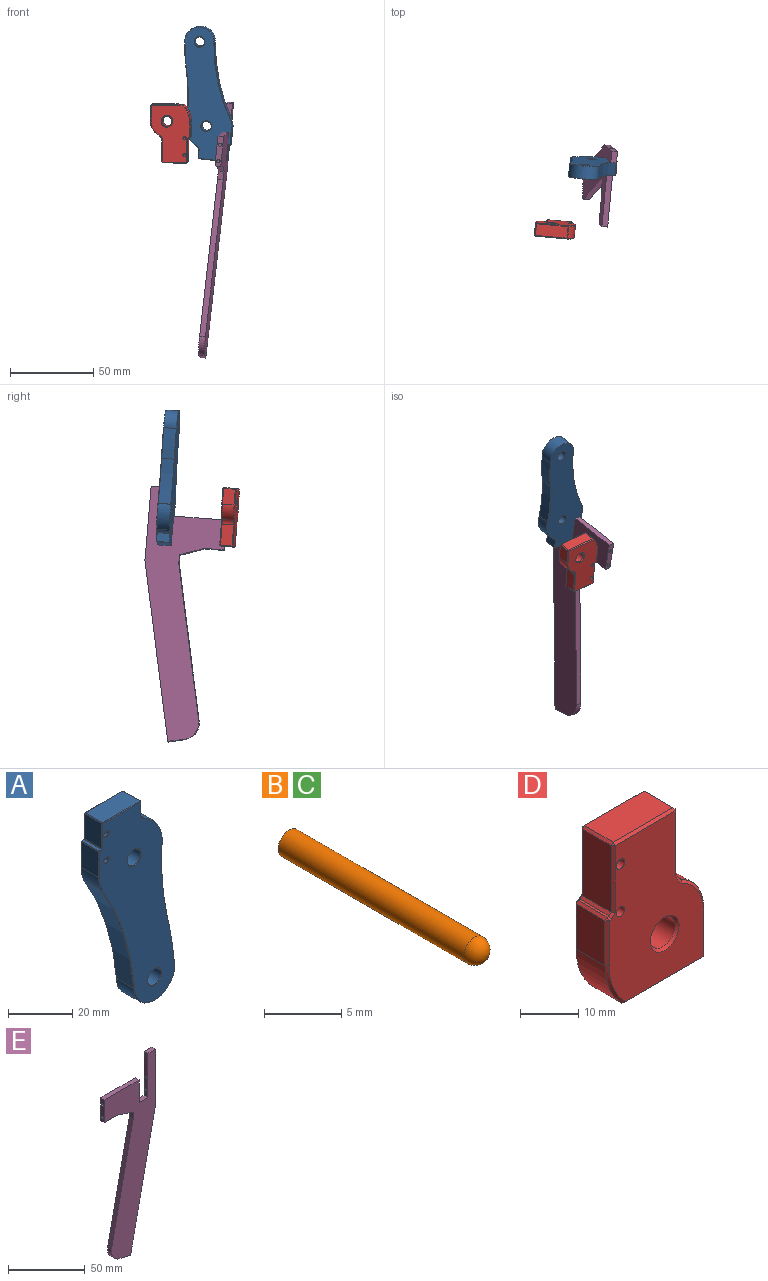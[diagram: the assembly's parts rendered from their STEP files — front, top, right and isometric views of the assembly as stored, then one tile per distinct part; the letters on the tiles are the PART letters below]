
ASSEMBLY  parts=5 mates=4
PART A: 80 faces, bbox 33.5x8x79 mm
  f0: plane 16.6x7.6mm, normal (0,0,1), area 126.2mm2, adj f45,f46,f56,f57
  f1: plane 9.6x7.6mm, normal (-1,0,0), area 73mm2, adj f55,f56,f65,f66
  f2: plane 7.6x1.1mm, normal (0,0,1), area 8.4mm2, adj f60,f65,f68,f71
  f3: plane 9.8x7.6mm, normal (-1,0,0), area 74.5mm2, adj f4,f59,f67,f68
  f4: cylinder r=14mm len=7.6mm, axis (0,1,0), area 37.8mm2, adj f3,f53,f54,f63
  f5: cylinder r=106mm len=45.07mm, axis (0,1,0), area 363.2mm2, adj f43,f44,f52,f53
  f6: cylinder r=9mm len=18mm, axis (0,1,0), area 234mm2, adj f33,f34,f42,f43
  f7: cylinder r=130mm len=18.19mm, axis (0,1,0), area 140.3mm2, adj f24,f25,f32,f33
  f8: cylinder r=106mm len=26.98mm, axis (0,1,0), area 206.3mm2, adj f18,f22,f23,f24
  f9: cylinder r=14mm len=14.77mm, axis (0,1,0), area 134.6mm2, adj f10,f21,f22,f31
  f10: cylinder r=4mm len=7.6mm, axis (0,1,0), area 20.1mm2, adj f9,f26,f36,f37
  f11: cylinder r=1mm len=7.6mm, axis (0,1,0), area 47.8mm2, adj f72,f74
  f12: cylinder r=1mm len=7.6mm, axis (0,1,0), area 47.8mm2, adj f73,f75
  f13: cylinder r=3mm len=7.6mm, axis (0,1,0), area 143.3mm2, adj f77,f78
  f14: cylinder r=3mm len=7.6mm, axis (0,1,0), area 143.3mm2, adj f76,f79
  f15: plane 7.6x5.37mm, normal (1,0,0), area 40.8mm2, adj f35,f36,f46,f47
  f16: plane 78.6x33.1mm, normal (0,-1,0), area 1498.9mm2, adj f23,f27,f28,f31,f32,f37,f38,f41
  f17: plane 78.6x33.1mm, normal (0,1,0), area 1498.9mm2, adj f18,f19,f20,f21,f25,f26,f29,f30
  f18: cone r=106.2mm half-angle=45deg, axis (0,1,0), area 7.7mm2, adj f8,f17,f19,f20
  f19: plane 0.2x0.2mm, normal (0.7,0.71,-0.07), area 0mm2, adj f17,f18,f21,f22
  f20: plane 0.2x0.2mm, normal (0.69,0.71,0.16), area 0mm2, adj f17,f18,f24,f25
  f21: cone r=14mm half-angle=45deg, axis (0,-1,0), area 5mm2, adj f9,f17,f19,f26
  f22: plane 7.6x0.02mm, normal (0.99,0,-0.1), area 0.2mm2, adj f8,f9,f19,f27
  f23: cone r=106mm half-angle=45deg, axis (0,-1,0), area 7.7mm2, adj f8,f16,f27,f28
  f24: plane 7.6x0.01mm, normal (0.97,0,0.22), area 0mm2, adj f7,f8,f20,f28
  f25: cone r=130mm half-angle=45deg, axis (0,-1,0), area 5.2mm2, adj f7,f17,f20,f29
  f26: cone r=4.2mm half-angle=45deg, axis (0,1,0), area 0.8mm2, adj f10,f17,f21,f30
  f27: plane 0.2x0.2mm, normal (0.7,-0.71,-0.07), area 0mm2, adj f16,f22,f23,f31
  f28: plane 0.2x0.2mm, normal (0.69,-0.71,0.16), area 0mm2, adj f16,f23,f24,f32
  f29: plane 0.21x0.2mm, normal (0.7,0.71,0.13), area 0mm2, adj f17,f25,f33,f34
  f30: plane 0.22x0.2mm, normal (0.7,0.7,0.16), area 0mm2, adj f17,f26,f35,f36
  f31: cone r=13.8mm half-angle=45deg, axis (0,1,0), area 5mm2, adj f9,f16,f27,f37
  f32: cone r=129.8mm half-angle=45deg, axis (0,1,0), area 5.2mm2, adj f7,f16,f28,f38
  f33: plane 7.6x0.04mm, normal (0.98,0,0.19), area 0.3mm2, adj f6,f7,f29,f38
  f34: cone r=9mm half-angle=45deg, axis (0,-1,0), area 8.6mm2, adj f6,f17,f29,f39
  f35: plane 5.37x0.2mm, normal (0.71,0.71,0), area 1.5mm2, adj f15,f17,f30,f40
  f36: plane 7.6x0.09mm, normal (0.98,0,0.22), area 0.7mm2, adj f10,f15,f30,f41
  f37: cone r=4mm half-angle=45deg, axis (0,-1,0), area 0.8mm2, adj f10,f16,f31,f41
  f38: plane 0.21x0.2mm, normal (0.7,-0.71,0.13), area 0mm2, adj f16,f32,f33,f42
  f39: plane 0.2x0.2mm, normal (-0.71,0.71,-0.03), area 0mm2, adj f17,f34,f43,f44
  f40: plane 0.2x0.2mm, normal (0.58,0.58,0.58), area 0mm2, adj f35,f45,f46
  f41: plane 0.22x0.2mm, normal (0.7,-0.7,0.16), area 0mm2, adj f16,f36,f37,f47
  f42: cone r=8.8mm half-angle=45deg, axis (0,1,0), area 8.6mm2, adj f6,f16,f38,f48
  f43: plane 7.6x0.02mm, normal (-1,0,-0.04), area 0.1mm2, adj f5,f6,f39,f48
  f44: cone r=106.2mm half-angle=45deg, axis (0,1,0), area 13.5mm2, adj f5,f17,f39,f49
  f45: plane 16.6x0.2mm, normal (0,0.71,0.71), area 4.7mm2, adj f0,f17,f40,f50
  f46: plane 7.6x0.2mm, normal (0.71,0,0.71), area 2.1mm2, adj f0,f15,f40,f51
  f47: plane 5.37x0.2mm, normal (0.71,-0.71,0), area 1.5mm2, adj f15,f16,f41,f51
  f48: plane 0.2x0.2mm, normal (-0.71,-0.71,-0.03), area 0mm2, adj f16,f42,f43,f52
  f49: plane 0.2x0.19mm, normal (-0.64,0.71,-0.31), area 0mm2, adj f44,f53,f54
  f50: plane 0.2x0.2mm, normal (-0.58,0.58,0.58), area 0mm2, adj f45,f55,f56
  f51: plane 0.2x0.2mm, normal (0.58,-0.58,0.58), area 0mm2, adj f46,f47,f57
  f52: cone r=106mm half-angle=45deg, axis (0,-1,0), area 13.5mm2, adj f5,f16,f48,f58
  f53: plane 7.6x0.03mm, normal (-0.9,0,-0.43), area 0.3mm2, adj f4,f5,f49,f58
  f54: cone r=14mm half-angle=45deg, axis (0,-1,0), area 1.4mm2, adj f4,f17,f49,f59
  f55: plane 9.6x0.2mm, normal (-0.71,0.71,0), area 2.7mm2, adj f1,f17,f50,f61
  f56: plane 7.6x0.2mm, normal (-0.71,0,0.71), area 2.1mm2, adj f0,f1,f50,f62
  f57: plane 16.6x0.2mm, normal (0,-0.71,0.71), area 4.7mm2, adj f0,f16,f51,f62
  f58: plane 0.2x0.19mm, normal (-0.64,-0.71,-0.31), area 0mm2, adj f52,f53,f63
  f59: plane 9.8x0.2mm, normal (-0.71,0.71,0), area 2.8mm2, adj f3,f17,f54,f64
  f60: plane 1.1x0.2mm, normal (0,0.71,0.71), area 0.3mm2, adj f2,f17,f61,f64
  f61: plane 0.4x0.4mm, normal (-0.58,0.58,0.58), area 0.1mm2, adj f17,f55,f60,f65
  f62: plane 0.2x0.2mm, normal (-0.58,-0.58,0.58), area 0mm2, adj f56,f57,f66
  f63: cone r=13.8mm half-angle=45deg, axis (0,1,0), area 1.4mm2, adj f4,f16,f58,f67
  f64: plane 0.2x0.2mm, normal (-0.58,0.58,0.58), area 0mm2, adj f59,f60,f68
  f65: plane 7.6x0.2mm, normal (-0.71,0,0.71), area 2.1mm2, adj f1,f2,f61,f69
  f66: plane 9.6x0.2mm, normal (-0.71,-0.71,0), area 2.7mm2, adj f1,f16,f62,f69
  f67: plane 9.8x0.2mm, normal (-0.71,-0.71,0), area 2.8mm2, adj f3,f16,f63,f70
  f68: plane 7.6x0.2mm, normal (-0.71,0,0.71), area 2.1mm2, adj f2,f3,f64,f70
  f69: plane 0.4x0.4mm, normal (-0.58,-0.58,0.58), area 0.1mm2, adj f16,f65,f66,f71
  f70: plane 0.2x0.2mm, normal (-0.58,-0.58,0.58), area 0mm2, adj f67,f68,f71
  f71: plane 1.1x0.2mm, normal (0,-0.71,0.71), area 0.3mm2, adj f2,f16,f69,f70
  f72: cone r=1mm half-angle=45deg, axis (0,-1,0), area 2mm2, adj f11,f16
  f73: cone r=1mm half-angle=45deg, axis (0,-1,0), area 2mm2, adj f12,f16
  f74: cone r=1.2mm half-angle=45deg, axis (0,1,0), area 2mm2, adj f11,f17
  f75: cone r=1.2mm half-angle=45deg, axis (0,1,0), area 2mm2, adj f12,f17
  f76: cone r=3mm half-angle=45deg, axis (0,-1,0), area 5.5mm2, adj f14,f16
  f77: cone r=3mm half-angle=45deg, axis (0,-1,0), area 5.5mm2, adj f13,f16
  f78: cone r=3.2mm half-angle=45deg, axis (0,1,0), area 5.5mm2, adj f13,f17
  f79: cone r=3.2mm half-angle=45deg, axis (0,1,0), area 5.5mm2, adj f14,f17
PART B: 3 faces, bbox 2x18x2 mm
  f0: cylinder r=1mm len=17mm, axis (0,-1,0), area 106.8mm2, adj f1,f2
  f1: plane 2x2mm, normal (0,1,0), area 3.1mm2, adj f0
  f2: sphere r=1mm, area 6.3mm2, adj f0
PART C: same geometry as B
PART D: 61 faces, bbox 24x8x35 mm
  f0: plane 34x23mm, normal (0,-1,0), area 580.8mm2, adj f10,f11,f15,f16,f21,f22,f27,f31
  f1: plane 9.5x7mm, normal (1,0,0), area 66.5mm2, adj f2,f30,f31,f39
  f2: cylinder r=10mm len=8.93mm, axis (0,1,0), area 77.3mm2, adj f1,f36,f44,f45
  f3: cylinder r=4mm len=7mm, axis (0,1,0), area 22.9mm2, adj f45,f46,f54,f55
  f4: plane 12.62x7mm, normal (1,0,0), area 88.3mm2, adj f47,f52,f55,f58
  f5: plane 14.5x7mm, normal (0,0,1), area 101.5mm2, adj f41,f42,f52,f53
  f6: plane 14x7mm, normal (-1,0,0), area 98mm2, adj f32,f33,f42,f43
  f7: plane 7x0.5mm, normal (0,0,1), area 3.5mm2, adj f22,f23,f33,f34
  f8: plane 9.5x7mm, normal (-1,0,0), area 66.5mm2, adj f9,f16,f23,f24
  f9: cylinder r=14mm len=9.85mm, axis (0,1,0), area 76.5mm2, adj f8,f15,f19,f20
  f10: cylinder r=1mm len=8mm, axis (0,1,0), area 50.3mm2, adj f0,f14
  f11: cylinder r=1mm len=8mm, axis (0,1,0), area 50.3mm2, adj f0,f14
  f12: plane 19.09x7mm, normal (0,0,-1), area 133.6mm2, adj f20,f21,f29,f30
  f13: cylinder r=3mm len=7mm, axis (0,1,0), area 131.9mm2, adj f59,f60
  f14: plane 34x23mm, normal (0,1,0), area 580.8mm2, adj f10,f11,f19,f24,f29,f34,f38,f39
  f15: cone r=13.5mm half-angle=45deg, axis (0,1,0), area 7.6mm2, adj f0,f9,f16,f17
  f16: plane 9.5x0.5mm, normal (-0.71,-0.71,0), area 6.7mm2, adj f0,f8,f15,f18
  f17: plane 0.5x0.5mm, normal (-0.28,-0.68,-0.68), area 0.1mm2, adj f15,f20,f21
  f18: plane 0.5x0.5mm, normal (-0.58,-0.58,0.58), area 0.2mm2, adj f16,f22,f23
  f19: cone r=14mm half-angle=45deg, axis (0,-1,0), area 7.6mm2, adj f9,f14,f24,f25
  f20: plane 7x0.36mm, normal (-0.38,0,-0.92), area 2.7mm2, adj f9,f12,f17,f25
  f21: plane 19.09x0.5mm, normal (0,-0.71,-0.71), area 13.5mm2, adj f0,f12,f17,f26
  f22: plane 0.5x0.5mm, normal (0,-0.71,0.71), area 0.4mm2, adj f0,f7,f18,f27
  f23: plane 7x0.5mm, normal (-0.71,0,0.71), area 4.9mm2, adj f7,f8,f18,f28
  f24: plane 9.5x0.5mm, normal (-0.71,0.71,0), area 6.7mm2, adj f8,f14,f19,f28
  f25: plane 0.5x0.5mm, normal (-0.28,0.68,-0.68), area 0.1mm2, adj f19,f20,f29
  f26: plane 0.5x0.5mm, normal (0.58,-0.58,-0.58), area 0.2mm2, adj f21,f30,f31
  f27: plane 1x1mm, normal (-0.58,-0.58,0.58), area 0.6mm2, adj f0,f22,f32,f33
  f28: plane 0.5x0.5mm, normal (-0.58,0.58,0.58), area 0.2mm2, adj f23,f24,f34
  f29: plane 19.09x0.5mm, normal (0,0.71,-0.71), area 13.5mm2, adj f12,f14,f25,f35
  f30: plane 7x0.5mm, normal (0.71,0,-0.71), area 4.9mm2, adj f1,f12,f26,f35
  f31: plane 9.5x0.5mm, normal (0.71,-0.71,0), area 6.7mm2, adj f0,f1,f26,f36
  f32: plane 14x0.5mm, normal (-0.71,-0.71,0), area 9.9mm2, adj f0,f6,f27,f37
  f33: plane 7x0.5mm, normal (-0.71,0,0.71), area 4.9mm2, adj f6,f7,f27,f38
  f34: plane 0.5x0.5mm, normal (0,0.71,0.71), area 0.4mm2, adj f7,f14,f28,f38
  f35: plane 0.5x0.5mm, normal (0.58,0.58,-0.58), area 0.2mm2, adj f29,f30,f39
  f36: cone r=9.5mm half-angle=45deg, axis (0,1,0), area 7.6mm2, adj f0,f2,f31,f40
  f37: plane 0.5x0.5mm, normal (-0.58,-0.58,0.58), area 0.2mm2, adj f32,f41,f42
  f38: plane 1x1mm, normal (-0.58,0.58,0.58), area 0.6mm2, adj f14,f33,f34,f43
  f39: plane 9.5x0.5mm, normal (0.71,0.71,0), area 6.7mm2, adj f1,f14,f35,f44
  f40: plane 0.51x0.5mm, normal (0.39,-0.7,0.59), area 0.1mm2, adj f0,f36,f45,f46
  f41: plane 14.5x0.5mm, normal (0,-0.71,0.71), area 10.3mm2, adj f0,f5,f37,f48
  f42: plane 7x0.5mm, normal (-0.71,0,0.71), area 4.9mm2, adj f5,f6,f37,f49
  f43: plane 14x0.5mm, normal (-0.71,0.71,0), area 9.9mm2, adj f6,f14,f38,f49
  f44: cone r=10mm half-angle=45deg, axis (0,-1,0), area 7.6mm2, adj f2,f14,f39,f50
  f45: plane 7x0.1mm, normal (0.55,0,0.83), area 0.9mm2, adj f2,f3,f40,f50
  f46: cone r=4mm half-angle=45deg, axis (0,-1,0), area 2.5mm2, adj f0,f3,f40,f51
  f47: plane 12.62x0.5mm, normal (0.71,-0.71,0), area 8.9mm2, adj f0,f4,f48,f51
  f48: plane 0.5x0.5mm, normal (0.58,-0.58,0.58), area 0.2mm2, adj f41,f47,f52
  f49: plane 0.5x0.5mm, normal (-0.58,0.58,0.58), area 0.2mm2, adj f42,f43,f53
  f50: plane 0.51x0.5mm, normal (0.39,0.7,0.59), area 0.1mm2, adj f14,f44,f45,f54
  f51: plane 0.5x0.5mm, normal (0.71,-0.71,0.02), area 0mm2, adj f0,f46,f47,f55
  f52: plane 7x0.5mm, normal (0.71,0,0.71), area 4.9mm2, adj f4,f5,f48,f56
  f53: plane 14.5x0.5mm, normal (0,0.71,0.71), area 10.3mm2, adj f5,f14,f49,f56
  f54: cone r=4.5mm half-angle=45deg, axis (0,1,0), area 2.5mm2, adj f3,f14,f50,f57
  f55: plane 7x0.02mm, normal (1,0,0.02), area 0.2mm2, adj f3,f4,f51,f57
  f56: plane 0.5x0.5mm, normal (0.58,0.58,0.58), area 0.2mm2, adj f52,f53,f58
  f57: plane 0.5x0.5mm, normal (0.71,0.71,0.02), area 0mm2, adj f14,f54,f55,f58
  f58: plane 12.62x0.5mm, normal (0.71,0.71,0), area 8.9mm2, adj f4,f14,f56,f57
  f59: cone r=3.5mm half-angle=45deg, axis (0,1,0), area 14.4mm2, adj f13,f14
  f60: cone r=3mm half-angle=45deg, axis (0,-1,0), area 14.4mm2, adj f0,f13
PART E: 26 faces, bbox 47x3.5x152.6 mm
  f0: plane 7x3.5mm, normal (0,0,1), area 24.5mm2, adj f1,f13,f14,f15
  f1: plane 35x3.5mm, normal (-1,0,0), area 116.2mm2, adj f0,f2,f14,f15,f20,f21
  f2: plane 8x3.5mm, normal (0,0,1), area 28mm2, adj f1,f3,f14,f15
  f3: plane 18x3.5mm, normal (1,0,0), area 56.7mm2, adj f2,f4,f14,f15,f17,f19
  f4: plane 32x3.5mm, normal (0,0,1), area 112mm2, adj f3,f5,f14,f15
  f5: plane 18x3.5mm, normal (-1,0,0), area 56.7mm2, adj f4,f6,f14,f15,f22,f24
  f6: plane 12x3.5mm, normal (0,0,-1), area 42mm2, adj f5,f7,f14,f15
  f7: plane 14.55x5mm, normal (-0.32,0,-0.95), area 53.9mm2, adj f6,f8,f14,f15
  f8: plane 5x3.5mm, normal (-1,0,0), area 17.5mm2, adj f7,f9,f14,f15
  f9: plane 93.66x19.91mm, normal (-0.98,0,0.21), area 335.1mm2, adj f8,f10,f14,f15
  f10: cylinder r=10mm len=11.86mm, axis (0,1,0), area 55mm2, adj f9,f11,f14,f15
  f11: plane 9.78x3.5mm, normal (-0.21,0,-0.98), area 35mm2, adj f10,f12,f14,f15
  f12: plane 107.6x22.87mm, normal (0.98,0,-0.21), area 385mm2, adj f11,f13,f14,f15
  f13: plane 45x3.5mm, normal (1,0,0), area 151.2mm2, adj f0,f12,f14,f15,f20,f21
  f14: plane 152.6x47mm, normal (0,-1,0), area 3197.9mm2, adj f0,f1,f2,f3,f4,f5,f6,f7
  f15: plane 152.6x47mm, normal (0,1,0), area 3197.9mm2, adj f0,f1,f2,f3,f4,f5,f6,f7
  f16: plane 2x2mm, normal (1,0,0), area 3.1mm2, adj f17
  f17: cylinder r=1mm len=5mm, axis (1,0,0), area 31.4mm2, adj f3,f16
  f18: plane 2x2mm, normal (1,0,0), area 3.1mm2, adj f19
  f19: cylinder r=1mm len=5mm, axis (1,0,0), area 31.4mm2, adj f3,f18
  f20: cylinder r=1mm len=7mm, axis (1,0,0), area 44mm2, adj f1,f13
  f21: cylinder r=1mm len=7mm, axis (1,0,0), area 44mm2, adj f1,f13
  f22: cylinder r=1mm len=12mm, axis (-1,0,0), area 75.4mm2, adj f5,f23
  f23: plane 2x2mm, normal (-1,0,0), area 3.1mm2, adj f22
  f24: cylinder r=1mm len=12mm, axis (-1,0,0), area 75.4mm2, adj f5,f25
  f25: plane 2x2mm, normal (-1,0,0), area 3.1mm2, adj f24
PLACE A rot(axis=(-0.04,-1,-0.04),174.2deg) t=(5.82,30.21,3.23)mm
PLACE B rot(axis=(0.51,0.65,-0.57),8.9deg) t=(52.05,15.91,-11.03)mm
PLACE C rot(axis=(0.51,0.65,-0.57),8.9deg) t=(51.1,16.75,-20.95)mm
PLACE D rot(axis=(-0.05,-1,-0.04),179.2deg) t=(-16,-7.88,1.01)mm
PLACE E rot(axis=(0.09,0.01,1),85.2deg) t=(20,33.42,36.87)mm
MATE planar E.f19 <-> A.f12  axis (0.09,0.99,0.07) through (18.44,20.04,15.73)mm
MATE pin_slot C.f0 <-> E.f17  axis (-0.09,-0.99,-0.07) through (18.87,35.77,6.93)mm
MATE planar D.f10 <-> E.f22  axis (0.09,0.99,0.07) through (-5.25,-9.24,5.81)mm
MATE pin_slot B.f0 <-> E.f19  axis (0.09,0.99,0.07) through (19.83,34.94,16.85)mm
